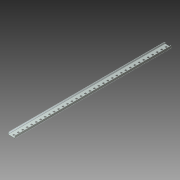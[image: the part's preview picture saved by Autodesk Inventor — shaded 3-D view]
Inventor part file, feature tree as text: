
AUTODESK INVENTOR PART (.ipt)
format: ipt  version: 2013 (Build 170138000, 138)  size: 443,904 bytes
history: native  units: in
note: dims shown in document units (in); Inventor stores cm internally (conversion verified against a paired STEP export)
features: other x39, extrude x35, sheet_metal_op x4, sketch x4, pattern_linear x2
ambient origin geometry x8: Origin, YZ Plane, XZ Plane, XY Plane, X Axis, Y Axis, Z Axis, Center Point
bodies: Solid1 (feature_tree)
feature tree (84):
  sheet_metal_op  "Face1"
  sheet_metal_op  "Flange1"
  other  "Corner Chamfer1"
  pattern_linear  "Rectangular Pattern1"  Spacing1=0.0235in  [1 undecoded]
  pattern_linear  "Rectangular Pattern2"  Spacing1=0.094in  [1 undecoded]
  sketch  "Sketch1"  dims[d0=0.867in]
  other  "Plate1"
  sketch  "Sketch2"  dims[d1=17.5in]
  other  "Plate2"
  sheet_metal_op  "Bend1"
  sheet_metal_op  "Corner1"
  sketch  "Sketch4"  dims[d2=0.03in]
  sketch  "Sketch5"  dims[d3=0.047in d4=0.0235in d5=0.094in d6=0.03in d7=0.222in d8=105.0deg d9=0.03in d10=0.188in d11=0.047in d12=0.03in d13=0.075in d14=0.25in d15=45.0deg d16=0.182in d17=0.047in d18=0.0in d19=0.02in d20=13.7795in d22=0.5in d23=0.179in d24=1.0in d25=0.0in d26=0.0in d27=0.0in d28=13.7795in d30=0.5in d31=0.0in d32=0.0in d33=0.0in d34=0.0in d35=0.0in d36=0.0in d37=0.0in d38=0.0in d39=0.0in d40=0.0in d41=0.0in d42=0.0in d43=0.0in d44=0.0in d45=0.0in d46=0.0in d47=0.0in d48=0.0in d49=0.0in d50=0.0in d51=0.0in d52=0.0in d53=0.0in d54=0.0in d55=0.0in d56=0.0in d57=0.0in d58=0.0in d59=0.0in d60=0.0in d61=0.0in d62=0.0in d63=0.0in d64=0.0in d65=0.0in d66=0.0in d67=0.0in d68=0.0in d69=0.0in d70=0.0in d71=0.0in d72=0.0in d73=0.0in d74=0.0in d75=0.0in d76=0.0in d77=0.0in d78=0.0in d79=0.0in d80=0.0in d81=0.0in d82=0.0in d83=0.0in d84=0.0in d85=0.0in d86=0.0in d87=0.0in d88=0.0in d89=0.0in d90=0.0in d91=0.0in d92=0.0in d93=0.0in d94=0.0in d95=0.0in d96=0.0in d97=0.0in d98=0.0in]
  other  "Srf1"
  other  "Srf2"
  other  "Srf3"
  other  "Srf4"
  other  "Srf5"
  other  "Srf6"
  other  "Srf7"
  other  "Srf8"
  other  "Srf9"
  other  "Srf10"
  other  "Srf11"
  other  "Srf12"
  other  "Srf13"
  other  "Srf14"
  other  "Srf15"
  other  "Srf16"
  other  "Srf17"
  other  "Srf18"
  other  "Srf19"
  other  "Srf20"
  other  "Srf21"
  other  "Srf22"
  other  "Srf23"
  other  "Srf24"
  other  "Srf25"
  other  "Srf26"
  other  "Srf27"
  other  "Srf28"
  other  "Srf29"
  other  "Srf30"
  other  "Srf31"
  other  "Srf32"
  other  "Srf33"
  other  "Srf34"
  other  "Srf35"
  other  "Cut1"
  extrude  "ExtrusionSrf1"  Depth=0.03in
  extrude  "ExtrusionSrf2"  Depth=0.222in TaperAngle=105.0deg
  extrude  "ExtrusionSrf3"  Depth=0.188in
  extrude  "ExtrusionSrf4"  Depth=0.047in
  extrude  "ExtrusionSrf5"  Depth=0.03in
  extrude  "ExtrusionSrf6"  Depth=0.075in TaperAngle=45.0deg
  extrude  "ExtrusionSrf7"  Depth=0.182in
  extrude  "ExtrusionSrf8"  Depth=0.047in
  extrude  "ExtrusionSrf9"  TaperAngle=0.0deg  [1 undecoded]
  extrude  "ExtrusionSrf10"  Depth=0.02in
  extrude  "ExtrusionSrf11"  Depth=13.7795in
  extrude  "ExtrusionSrf12"  Depth=0.179in
  extrude  "ExtrusionSrf13"  Depth=1.0in TaperAngle=0.0deg
  extrude  "ExtrusionSrf14"  TaperAngle=0.0deg  [1 undecoded]
  extrude  "ExtrusionSrf15"  Depth=13.7795in
  extrude  "ExtrusionSrf16"  [1 undecoded]
  extrude  "ExtrusionSrf17"  [1 undecoded]
  extrude  "ExtrusionSrf18"  [1 undecoded]
  extrude  "ExtrusionSrf19"  [1 undecoded]
  extrude  "ExtrusionSrf20"  [1 undecoded]
  extrude  "ExtrusionSrf21"  [1 undecoded]
  extrude  "ExtrusionSrf22"  [1 undecoded]
  extrude  "ExtrusionSrf23"  [1 undecoded]
  extrude  "ExtrusionSrf24"  [1 undecoded]
  extrude  "ExtrusionSrf25"  [1 undecoded]
  extrude  "ExtrusionSrf26"  [1 undecoded]
  extrude  "ExtrusionSrf27"  [1 undecoded]
  extrude  "ExtrusionSrf28"  [1 undecoded]
  extrude  "ExtrusionSrf29"  [1 undecoded]
  extrude  "ExtrusionSrf30"  [1 undecoded]
  extrude  "ExtrusionSrf31"  [1 undecoded]
  extrude  "ExtrusionSrf32"  [1 undecoded]
  extrude  "ExtrusionSrf33"  [1 undecoded]
  extrude  "ExtrusionSrf34"  [1 undecoded]
  extrude  "ExtrusionSrf35"  [1 undecoded]
note: 24 required parameter values undecoded (feature->parameter linkage not recoverable at this tier; creation-order binding heuristic only, values carry confidence <= 0.55)
